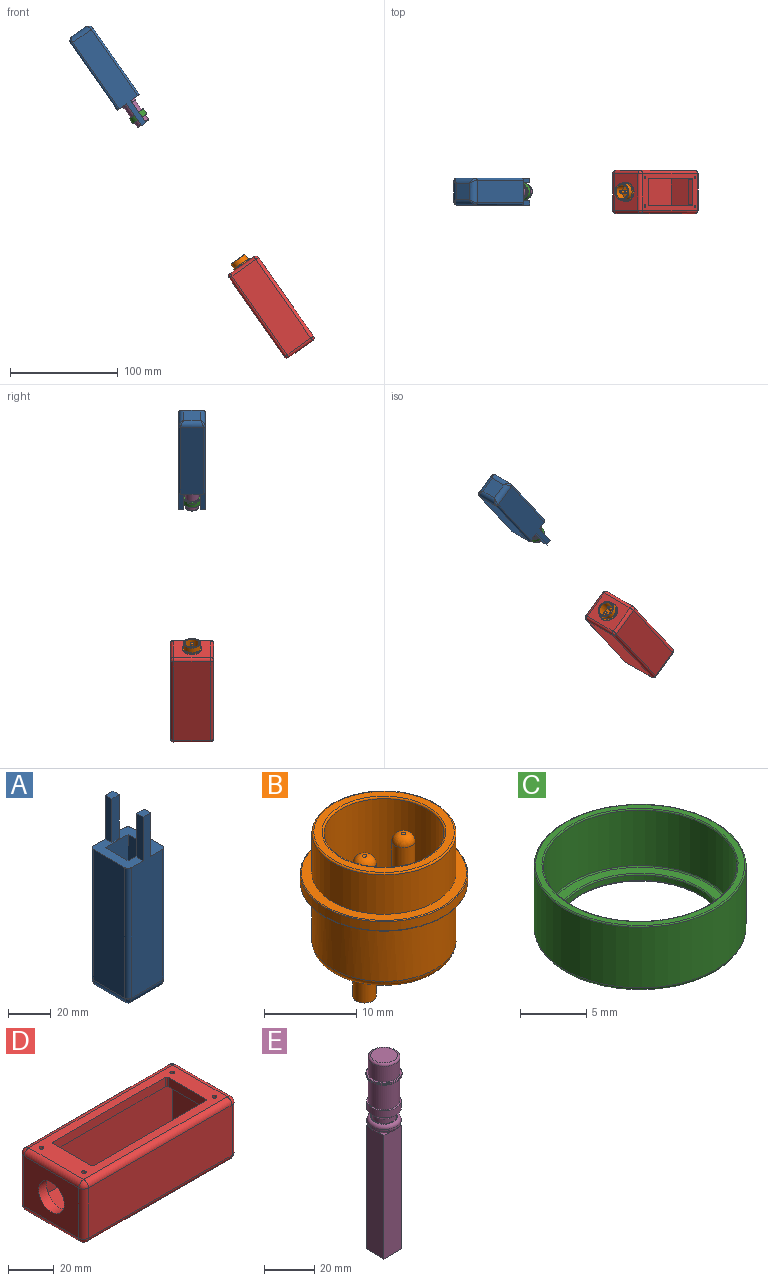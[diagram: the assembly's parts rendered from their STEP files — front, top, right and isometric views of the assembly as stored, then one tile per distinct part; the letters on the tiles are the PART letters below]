
ASSEMBLY  parts=5 mates=5
PART A: 31 faces, bbox 25x25x105 mm
  f0: plane 25x25mm, normal (0,0,1), area 354.4mm2, adj f1,f2,f3,f4,f6,f7,f8,f9
  f1: plane 100x21mm, normal (0,1,0), area 1700mm2, adj f0,f11,f15,f17,f23,f24,f26
  f2: plane 75x21mm, normal (1,0,0), area 1575mm2, adj f0,f12,f17,f21
  f3: plane 100x21mm, normal (0,-1,0), area 1700mm2, adj f0,f14,f19,f21,f27,f29,f30
  f4: plane 75x21mm, normal (-1,0,0), area 1575mm2, adj f0,f13,f15,f19
  f5: plane 15x15mm, normal (0,0,-1), area 225mm2, adj f11,f12,f13,f14
  f6: plane 75x15mm, normal (-1,0,0), area 1125mm2, adj f0,f7,f9,f10
  f7: plane 75x15mm, normal (0,1,0), area 1125mm2, adj f0,f6,f8,f10
  f8: plane 75x15mm, normal (1,0,0), area 1125mm2, adj f0,f7,f9,f10
  f9: plane 75x15mm, normal (0,-1,0), area 1125mm2, adj f0,f6,f8,f10
  f10: plane 15x15mm, normal (0,0,1), area 225mm2, adj f6,f7,f8,f9
  f11: cylinder r=5mm len=21mm, axis (-1,0,0), area 147.8mm2, adj f1,f5,f16,f18
  f12: cylinder r=5mm len=21mm, axis (0,1,0), area 147.8mm2, adj f2,f5,f18,f22
  f13: cylinder r=5mm len=21mm, axis (0,-1,0), area 147.8mm2, adj f4,f5,f16,f20
  f14: cylinder r=5mm len=21mm, axis (1,0,0), area 147.8mm2, adj f3,f5,f20,f22
  f15: cylinder r=2mm len=75mm, axis (0,0,1), area 235.6mm2, adj f0,f1,f4,f16
  f16: bspline ~5.91x5mm, area 16.7mm2, adj f11,f13,f15
  f17: cylinder r=2mm len=75mm, axis (0,0,-1), area 235.6mm2, adj f0,f1,f2,f18
  f18: bspline ~5.91x5mm, area 16.7mm2, adj f11,f12,f17
  f19: cylinder r=2mm len=75mm, axis (0,0,-1), area 235.6mm2, adj f0,f3,f4,f20
  f20: bspline ~5.91x5mm, area 16.7mm2, adj f13,f14,f19
  f21: cylinder r=2mm len=75mm, axis (0,0,1), area 235.6mm2, adj f0,f2,f3,f22
  f22: bspline ~5.91x5mm, area 16.7mm2, adj f12,f14,f21
  f23: plane 25x4.22mm, normal (1,0,0), area 105.4mm2, adj f0,f1,f25,f26
  f24: plane 25x4.22mm, normal (-1,0,0), area 105.4mm2, adj f0,f1,f25,f26
  f25: plane 25x5mm, normal (0,-1,0), area 125mm2, adj f0,f23,f24,f26
  f26: plane 5x4.22mm, normal (0,0,1), area 21.1mm2, adj f1,f23,f24,f25
  f27: plane 25x4.22mm, normal (1,0,0), area 105.4mm2, adj f0,f3,f28,f30
  f28: plane 25x5mm, normal (0,1,0), area 125mm2, adj f0,f27,f29,f30
  f29: plane 25x4.22mm, normal (-1,0,0), area 105.4mm2, adj f0,f3,f28,f30
  f30: plane 5x4.22mm, normal (0,0,1), area 21.1mm2, adj f3,f27,f28,f29
PART B: 24 faces, bbox 19.6x19.6x20.3 mm
  f0: cylinder r=7.8mm len=15.6mm, axis (0,0,-1), area 254.8mm2, adj f4,f19
  f1: plane 15.2x15.2mm, normal (0,0,1), area 40.4mm2, adj f19,f20
  f2: cylinder r=9.05mm len=18.1mm, axis (0,0,1), area 68.2mm2, adj f21,f23
  f3: plane 17.9x17.9mm, normal (0,0,-1), area 60.5mm2, adj f5,f21
  f4: plane 17.9x17.9mm, normal (0,0,1), area 60.5mm2, adj f0,f23
  f5: cylinder r=7.8mm len=15.6mm, axis (0,0,1), area 367.6mm2, adj f3,f22
  f6: plane 13.6x13.6mm, normal (0,0,-1), area 135.4mm2, adj f15,f17,f22
  f7: cylinder r=6.5mm len=13mm, axis (0,0,1), area 408.4mm2, adj f8,f20
  f8: plane 13x13mm, normal (0,0,1), area 122.9mm2, adj f7,f9,f11
  f9: cylinder r=1.25mm len=7.5mm, axis (0,0,-1), area 58.9mm2, adj f8,f13
  f10: plane 0.5x0.5mm, normal (0,0,1), area 0.2mm2, adj f13
  f11: cylinder r=1.25mm len=7.5mm, axis (0,0,-1), area 58.9mm2, adj f8,f14
  f12: plane 0.5x0.5mm, normal (0,0,1), area 0.2mm2, adj f14
  f13: torus R=0.25mm, axis (0,0,1), area 8.8mm2, adj f9,f10
  f14: torus R=0.25mm, axis (0,0,1), area 8.8mm2, adj f11,f12
  f15: cylinder r=1.25mm len=5mm, axis (0,0,1), area 39.3mm2, adj f6,f16
  f16: plane 2.5x2.5mm, normal (0,0,-1), area 4.9mm2, adj f15
  f17: cylinder r=1.25mm len=5mm, axis (0,0,1), area 39.3mm2, adj f6,f18
  f18: plane 2.5x2.5mm, normal (0,0,-1), area 4.9mm2, adj f17
  f19: torus R=7.6mm, axis (0,0,1), area 15.3mm2, adj f0,f1
  f20: torus R=6.7mm, axis (0,0,1), area 13mm2, adj f1,f7
  f21: torus R=8.95mm, axis (0,0,-1), area 8.9mm2, adj f2,f3
  f22: torus R=6.8mm, axis (0,0,-1), area 73.4mm2, adj f5,f6
  f23: torus R=8.95mm, axis (0,0,-1), area 8.9mm2, adj f2,f4
PART C: 12 faces, bbox 17.3x17.3x6 mm
  f0: torus R=7.2mm, axis (0,0,1), area 7.2mm2, adj f1,f11
  f1: plane 14.4x14.4mm, normal (0,0,1), area 33.1mm2, adj f0,f2
  f2: torus R=6.43mm, axis (0,0,1), area 6.3mm2, adj f1,f3
  f3: cylinder r=6.33mm len=12.65mm, axis (0,0,1), area 19.8mm2, adj f2,f4
  f4: torus R=6.43mm, axis (0,0,1), area 6.3mm2, adj f3,f5
  f5: plane 15.4x15.4mm, normal (0,0,-1), area 56.5mm2, adj f4,f6
  f6: torus R=7.7mm, axis (0,0,1), area 23.4mm2, adj f5,f7
  f7: cylinder r=8mm len=16mm, axis (0,0,1), area 281.5mm2, adj f6,f8
  f8: torus R=7.9mm, axis (0,0,1), area 7.9mm2, adj f7,f9
  f9: plane 15.8x15.8mm, normal (0,0,1), area 24.1mm2, adj f8,f10
  f10: torus R=7.4mm, axis (0,0,1), area 7.2mm2, adj f9,f11
  f11: cylinder r=7.3mm len=14.6mm, axis (0,0,1), area 233.9mm2, adj f0,f10
PART D: 45 faces, bbox 95x40x33 mm
  f0: plane 85x30mm, normal (0,0,-1), area 744.1mm2, adj f1,f2,f3,f4,f5,f6,f7,f11
  f1: cylinder r=1mm len=5mm, axis (0,0,-1), area 7.9mm2, adj f0,f2,f11,f17
  f2: plane 23.2x5mm, normal (-1,0,0), area 116mm2, adj f0,f1,f3,f17
  f3: cylinder r=1mm len=5mm, axis (0,0,-1), area 7.9mm2, adj f0,f2,f4,f17
  f4: plane 69.2x5mm, normal (0,1,0), area 346mm2, adj f0,f3,f5,f17
  f5: cylinder r=1mm len=5mm, axis (0,0,-1), area 7.9mm2, adj f0,f4,f6,f17
  f6: plane 23.2x5mm, normal (1,0,0), area 116mm2, adj f0,f5,f7,f17
  f7: cylinder r=1mm len=5mm, axis (0,0,-1), area 7.9mm2, adj f0,f6,f11,f17
  f8: plane 89x27mm, normal (0,-1,0), area 2403mm2, adj f27,f28,f37,f38
  f9: plane 34x27mm, normal (1,0,0), area 918mm2, adj f24,f28,f29,f30
  f10: plane 89x27mm, normal (0,1,0), area 2403mm2, adj f30,f31,f39,f40
  f11: plane 69.2x5mm, normal (0,-1,0), area 346mm2, adj f0,f1,f7,f17
  f12: cylinder r=1mm len=5mm, axis (0,0,-1), area 31.4mm2, adj f0,f17
  f13: cylinder r=1mm len=5mm, axis (0,0,-1), area 31.4mm2, adj f0,f17
  f14: cylinder r=1mm len=5mm, axis (0,0,-1), area 31.4mm2, adj f0,f17
  f15: plane 34x27mm, normal (-1,0,0), area 716.9mm2, adj f32,f37,f40,f43,f44
  f16: cylinder r=1mm len=5mm, axis (0,0,-1), area 31.4mm2, adj f0,f17
  f17: plane 89x34mm, normal (0,0,1), area 1220.1mm2, adj f1,f2,f3,f4,f5,f6,f7,f11
  f18: plane 30x23mm, normal (1,0,0), area 488.9mm2, adj f0,f19,f21,f22,f44
  f19: plane 85x23mm, normal (0,-1,0), area 1955mm2, adj f0,f18,f20,f22
  f20: plane 30x23mm, normal (-1,0,0), area 690mm2, adj f0,f19,f21,f22
  f21: plane 85x23mm, normal (0,1,0), area 1955mm2, adj f0,f18,f20,f22
  f22: plane 85x30mm, normal (0,0,1), area 2550mm2, adj f18,f19,f20,f21
  f23: plane 89x34mm, normal (0,0,-1), area 3026mm2, adj f29,f38,f39,f43
  f24: cylinder r=3mm len=34mm, axis (0,-1,0), area 160.2mm2, adj f9,f17,f25,f26
  f25: sphere r=3mm, area 14.1mm2, adj f24,f27,f28
  f26: sphere r=3mm, area 14.1mm2, adj f24,f30,f31
  f27: cylinder r=3mm len=89mm, axis (-1,0,0), area 419.4mm2, adj f8,f17,f25,f33
  f28: cylinder r=3mm len=27mm, axis (0,0,1), area 127.2mm2, adj f8,f9,f25,f34
  f29: cylinder r=3mm len=34mm, axis (0,-1,0), area 160.2mm2, adj f9,f23,f34,f35
  f30: cylinder r=3mm len=27mm, axis (0,0,-1), area 127.2mm2, adj f9,f10,f26,f35
  f31: cylinder r=3mm len=89mm, axis (1,0,0), area 419.4mm2, adj f10,f17,f26,f36
  f32: cylinder r=3mm len=34mm, axis (0,1,0), area 160.2mm2, adj f15,f17,f33,f36
  f33: sphere r=3mm, area 14.1mm2, adj f27,f32,f37
  f34: sphere r=3mm, area 14.1mm2, adj f28,f29,f38
  f35: sphere r=3mm, area 14.1mm2, adj f29,f30,f39
  f36: sphere r=3mm, area 14.1mm2, adj f31,f32,f40
  f37: cylinder r=3mm len=27mm, axis (0,0,-1), area 127.2mm2, adj f8,f15,f33,f41
  f38: cylinder r=3mm len=89mm, axis (-1,0,0), area 419.4mm2, adj f8,f23,f34,f41
  f39: cylinder r=3mm len=89mm, axis (1,0,0), area 419.4mm2, adj f10,f23,f35,f42
  f40: cylinder r=3mm len=27mm, axis (0,0,1), area 127.2mm2, adj f10,f15,f36,f42
  f41: sphere r=3mm, area 14.1mm2, adj f37,f38,f43
  f42: sphere r=3mm, area 14.1mm2, adj f39,f40,f43
  f43: cylinder r=3mm len=34mm, axis (0,1,0), area 160.2mm2, adj f15,f23,f41,f42
  f44: cylinder r=8mm len=16mm, axis (-1,0,0), area 251.3mm2, adj f15,f18
PART E: 32 faces, bbox 15.6x15.6x94.1 mm
  f0: cylinder r=6.3mm len=12.6mm, axis (0,0,-1), area 300.8mm2, adj f2,f5
  f1: plane 10.6x10.6mm, normal (0,0,1), area 88.2mm2, adj f2
  f2: torus R=5.3mm, axis (0,0,1), area 58.6mm2, adj f0,f1
  f3: cylinder r=7.2mm len=14.4mm, axis (0,0,1), area 27.1mm2, adj f6,f7
  f4: plane 14x14mm, normal (0,0,-1), area 33.2mm2, adj f7,f8
  f5: plane 14x14mm, normal (0,0,1), area 29.2mm2, adj f0,f6
  f6: torus R=7mm, axis (0,0,-1), area 14.1mm2, adj f3,f5
  f7: torus R=7mm, axis (0,0,-1), area 14.1mm2, adj f3,f4
  f8: cylinder r=6.2mm len=12.5mm, axis (0,0,1), area 486.9mm2, adj f4,f10
  f9: cylinder r=6.85mm len=13.7mm, axis (0,0,1), area 150.6mm2, adj f10,f11
  f10: plane 13.7x13.7mm, normal (0,0,1), area 26.6mm2, adj f8,f9
  f11: cone r=4.85mm half-angle=45deg, axis (0,0,1), area 104mm2, adj f9,f13
  f12: cylinder r=4.9mm len=9.8mm, axis (0,0,1), area 67.7mm2, adj f13,f16
  f13: plane 9.8x9.8mm, normal (0,0,1), area 1.5mm2, adj f11,f12
  f14: cylinder r=6.8mm len=13.6mm, axis (0,0,1), area 38.5mm2, adj f17,f18
  f15: plane 10.8x10.8mm, normal (0,0,-1), area 13.1mm2, adj f17,f19
  f16: plane 10.6x10.6mm, normal (0,0,1), area 12.8mm2, adj f12,f18
  f17: torus R=5.4mm, axis (0,0,-1), area 86.9mm2, adj f14,f15
  f18: torus R=5.3mm, axis (0,0,-1), area 92.6mm2, adj f14,f16
  f19: cylinder r=5mm len=10mm, axis (0,0,1), area 15.7mm2, adj f15,f25,f26,f27,f28
  f20: plane 10x10mm, normal (0,0,-1), area 100mm2, adj f21,f22,f23,f24
  f21: plane 60x10mm, normal (-1,0,0), area 600mm2, adj f20,f22,f24,f25,f28
  f22: plane 60x10mm, normal (0,-1,0), area 600mm2, adj f20,f21,f23,f25,f26
  f23: plane 60x10mm, normal (1,0,0), area 600mm2, adj f20,f22,f24,f26,f27
  f24: plane 60x10mm, normal (0,1,0), area 600mm2, adj f20,f21,f23,f27,f28
  f25: plane 5x5mm, normal (0,0,1), area 5.4mm2, adj f19,f21,f22
  f26: plane 5x5mm, normal (0,0,1), area 5.4mm2, adj f19,f22,f23
  f27: plane 5x5mm, normal (0,0,1), area 5.4mm2, adj f19,f23,f24
  f28: plane 5x5mm, normal (0,0,1), area 5.4mm2, adj f19,f21,f24
  f29: plane 5.5x5.5mm, normal (0,0,-1), area 23.8mm2, adj f30
  f30: cylinder r=2.75mm len=17mm, axis (0,0,-1), area 293.7mm2, adj f29,f31
  f31: plane 5.5x5.5mm, normal (0,0,1), area 23.8mm2, adj f30
PLACE A rot(axis=(0,1,0),145.1deg) t=(-373.51,-339.78,-142.79)mm
PLACE B rot(axis=(0.3,0,-0.95),180deg) t=(-275.95,-339.78,-282.43)mm
PLACE C rot(axis=(0,1,0),145.1deg) t=(-369.12,-339.78,-149.08)mm
PLACE D rot(axis=(0,1,0),55.1deg) t=(-237.11,-340.74,-317.94)mm
PLACE E rot(axis=(0,1,0),145.1deg) t=(-371.78,-339.78,-145.26)mm
MATE cylindrical A.f10 <-> E.f0  axis (0.57,0,-0.82) through (-423.63,-339.78,-71.06)mm
MATE planar D.f44 <-> B.f0  axis (-0.57,0,0.82) through (-275.15,-339.78,-283.58)mm
MATE cylindrical B.f0 <-> E.f0  axis (-0.57,0,0.82) through (-278.93,-339.78,-278.17)mm
MATE cylindrical E.f8 <-> C.f0  axis (0.57,0,-0.82) through (-375.94,-339.78,-139.32)mm
MATE cylindrical D.f44 <-> B.f0  axis (-0.57,0,0.82) through (-275.15,-339.78,-283.58)mm
